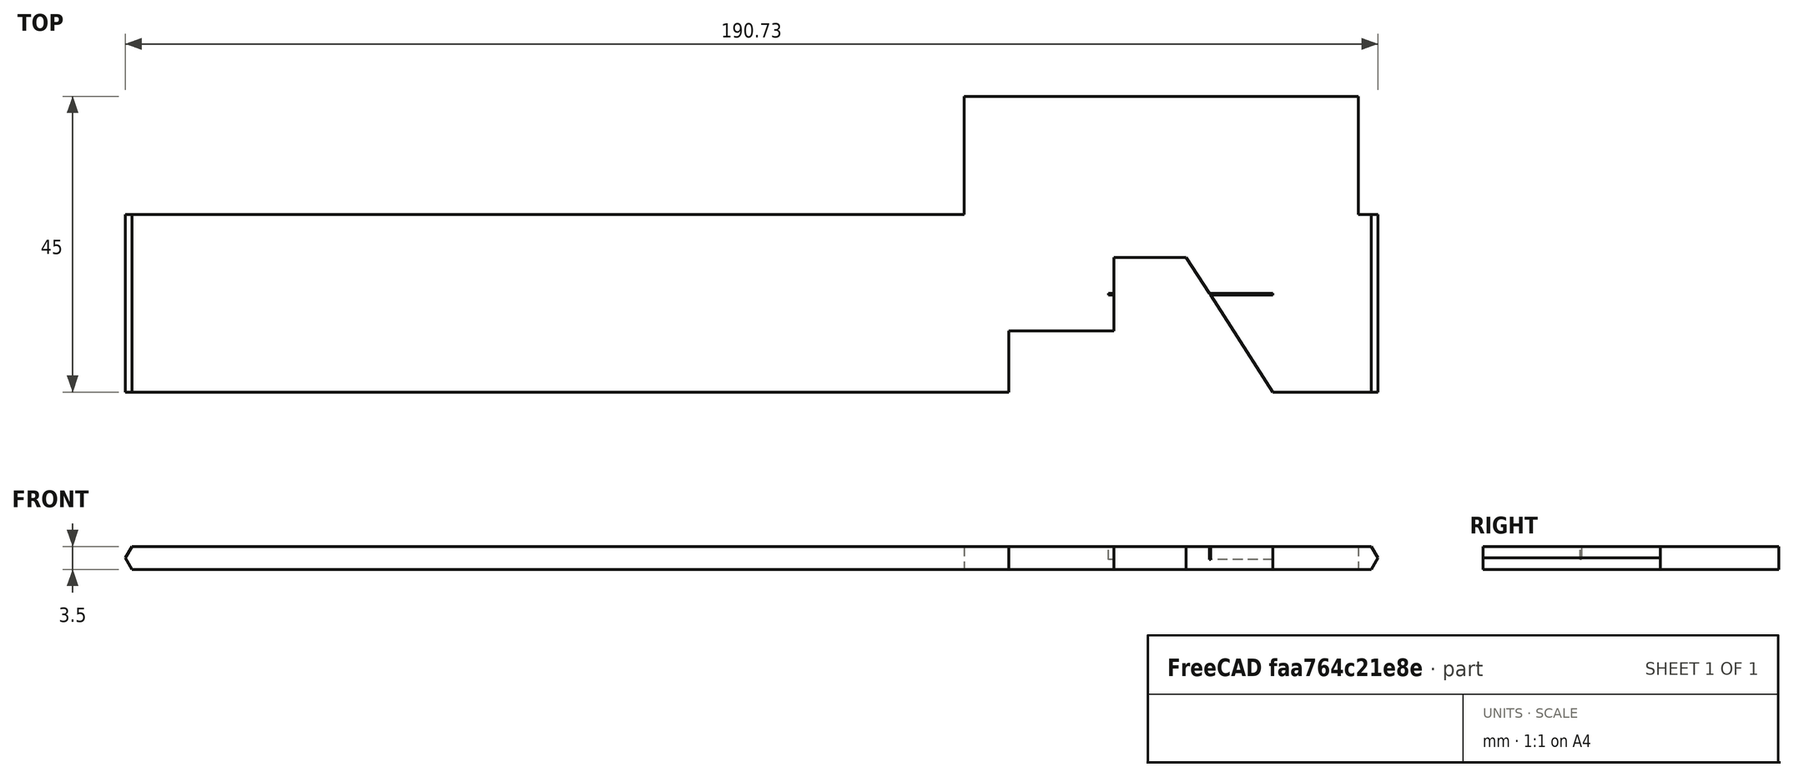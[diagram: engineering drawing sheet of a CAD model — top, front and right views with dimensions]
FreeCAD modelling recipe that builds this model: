
FCSTD DOCUMENT  (FreeCAD 0.22R35989 (Git))
Label: k1 inbetweener
License: All rights reserved
LicenseURL: http://en.wikipedia.org/wiki/All_rights_reserved
objects: Sketcher::SketchObject×3, Part::Feature×2, PartDesign::Pad×2, Mesh::Feature×1, Part::Refine×1, PartDesign::FeatureBase×1, PartDesign::Pocket×1, PartDesign::Body×1
note: 14 computed .brp shape members not serialized (recipe doc carries the construction recipe); baked Part::Feature solids carry a one-line shape summary decoded from their .brp

FEATURE [Mesh::Feature] k1_betweener  label="k1 betweener"
FEATURE [Part::Feature] k1_betweener001
  shape: bbox 190.7 x 45 x 3.5 mm, 68 faces, 0 solids (baked)
FEATURE [Part::Refine] k1_betweener002
  Source = -> k1_betweener001
FEATURE [Part::Feature] k1_betweener002_solid  label="k1_betweener002 (Solid)"
  shape: bbox 190.7 x 45 x 3.5 mm, 20 faces (baked)
FEATURE [PartDesign::FeatureBase] BaseFeature
  BaseFeature = -> k1_betweener002_solid
  Suppressed = false
FEATURE [Sketcher::SketchObject] Sketch
  ExternalGeometry = -> [BaseFeature]
  FullyConstrained = false
  MapMode = 5
  Placement = pos=(0,0,1.5) rot=(0,0,1;0rad)
  Support = -> [BaseFeature]
  sketch-geometry (4):
    g0: LineSegment StartX=54.99 StartY=-42.998 StartZ=0 EndX=79.99 EndY=-42.998 EndZ=0
    g1: LineSegment StartX=79.99 StartY=-42.998 StartZ=0 EndX=79.99 EndY=-38.2375 EndZ=0
    g2: LineSegment StartX=79.99 StartY=-38.2375 StartZ=0 EndX=54.99 EndY=-38.2375 EndZ=0
    g3: LineSegment StartX=54.99 StartY=-38.2375 StartZ=0 EndX=54.99 EndY=-42.998 EndZ=0
  constraints (10):
    c: Coincident(g0,g1)
    c: Coincident(g1,g2)
    c: Coincident(g2,g3)
    c: Coincident(g3,g0)
    c: Horizontal(g0)
    c: Horizontal(g2)
    c: Vertical(g1)
    c: Vertical(g3)
    c: Coincident(g0,g-3)
    c: PointOnObject(g1,g-5)
FEATURE [PartDesign::Pad] Pad
  BaseFeature = -> BaseFeature
  Direction = (0,0,1)
  Length = 2
  Length2 = 10
  Profile = -> Sketch
  ReferenceAxis = -> Sketch [N_Axis]
  Suppressed = false
  Type = 0
FEATURE [Sketcher::SketchObject] Sketch001
  ExternalGeometry = -> [Pad]
  FullyConstrained = true
  MapMode = 5
  Placement = pos=(0,0,3.5) rot=(0,0,1;0rad)
  Support = -> [Pad]
  sketch-geometry (4):
    g0: LineSegment StartX=38.498 StartY=-42.998 StartZ=0 EndX=38.498 EndY=-53 EndZ=0
    g1: LineSegment StartX=38.498 StartY=-53 StartZ=0 EndX=80.003 EndY=-53 EndZ=0
    g2: LineSegment StartX=80.003 StartY=-53 StartZ=0 EndX=80.003 EndY=-42.998 EndZ=0
    g3: LineSegment StartX=80.003 StartY=-42.998 StartZ=0 EndX=38.498 EndY=-42.998 EndZ=0
  constraints (10):
    c: Coincident(g0,g1)
    c: Coincident(g1,g2)
    c: Coincident(g2,g3)
    c: Coincident(g3,g0)
    c: Vertical(g0)
    c: Vertical(g2)
    c: Horizontal(g1)
    c: Horizontal(g3)
    c: Coincident(g0,g-5)
    c: Coincident(g1,g-3)
FEATURE [PartDesign::Pad] Pad001
  BaseFeature = -> Pad
  Direction = (0,0,1)
  Length = 3.5
  Length2 = 10
  Profile = -> Sketch001
  ReferenceAxis = -> Sketch001 [N_Axis]
  Reversed = true
  Suppressed = false
  Type = 0
FEATURE [Sketcher::SketchObject] Sketch002
  ExternalGeometry = -> [Pad001]
  FullyConstrained = true
  MapMode = 5
  Placement = pos=(0,0,3.5) rot=(0,0,1;0rad)
  Support = -> [Pad001]
  sketch-geometry (6):
    g0: LineSegment StartX=80.003 StartY=-53 StartZ=0 EndX=66.8 EndY=-32.5 EndZ=0
    g1: LineSegment StartX=66.8 StartY=-32.5 StartZ=0 EndX=55.8 EndY=-32.5 EndZ=0
    g2: LineSegment StartX=55.8 StartY=-32.5 StartZ=0 EndX=55.8 EndY=-43.7 EndZ=0
    g3: LineSegment StartX=55.8 StartY=-43.7 StartZ=0 EndX=39.8 EndY=-43.7 EndZ=0
    g4: LineSegment StartX=39.8 StartY=-43.7 StartZ=0 EndX=39.8 EndY=-53 EndZ=0
    g5: LineSegment StartX=39.8 StartY=-53 StartZ=0 EndX=80.003 EndY=-53 EndZ=0
  constraints (17):
    c: Coincident(g0,g-3)
    c: DistanceX(g0,g-4) = 29.2
    c: DistanceY(g0,g-5) = 24.5
    c: Coincident(g1,g0)
    c: Horizontal(g1)
    c: DistanceX(g1,g1) = 11
    c: Coincident(g2,g1)
    c: Vertical(g2)
    c: DistanceY(g2,g2) = 11.2
    c: Coincident(g3,g2)
    c: Horizontal(g3)
    c: DistanceX(g3,g3) = 16
    c: Coincident(g4,g3)
    c: PointOnObject(g4,g-6)
    c: Vertical(g4)
    c: Coincident(g5,g4)
    c: Coincident(g5,g0)
FEATURE [PartDesign::Pocket] Pocket
  BaseFeature = -> Pad001
  Direction = (0,0,-1)
  Length = 5
  Length2 = 5
  Profile = -> Sketch002
  ReferenceAxis = -> Sketch002 [N_Axis]
  Suppressed = false
  Type = 0
FEATURE [PartDesign::Body] Body
  BaseFeature = -> k1_betweener002_solid
  Group = -> [BaseFeature,Sketch,Pad,Sketch001,Pad001,Sketch002,Pocket]
  Origin = -> Origin
  Tip = -> Pocket
